# Revit family: Sanitary_Taps-Mixers_hansgrohe_75620XXX-Vivenis-Single-lever-shower-mix_NEW
name_source: partatom
category: Plumbing Fixtures
units: mm (PartAtom-declared; Revit-internal decimal feet)

## family parameters
Always vertical = No
Cut with Voids When Loaded = No
Maintain Annotation Orientation = No
OmniClass Number = 23.31.11.00
OmniClass Title = Faucets
Part Type = Normal
Room Calculation Point = No
Round Connector Dimension = Use Diameter
Shared = No
Work Plane-Based = Yes

## types (5) — shared parameters
Connector Description = Water Inlet 12.7 mm
Date Updated = 2024/11/15
Default Elevation = 1219 mm
Description = Vivenis Single lever shower mixer for exposed installation
Diameter = 13 mm
Manufacturer = Hansgrohe
Model = 75620XXX
Product Page URL = https://www.hansgrohe.com
Product data url = https://bimobject.com
URL = https://www.hansgrohe.com
Version = 2

## per-type parameters (varying)
| type | Material 1 |
| 000 Chrome | Hansgrohe - Metal - 000 Chrome |
| 140 Brushed Bronze | Hansgrohe - Metal - 140 Brushed Bronze |
| 340 Brushed Black Chrome | Hansgrohe - Metal - 340 Brushed Black Chrome |
| 670 Matte Black | Hansgrohe - Metal - 670 Matte Black |
| 700 Matte White | Hansgrohe - Metal - 700 Matte White |

## geometry (parser evidence)
native form markers: Sweep x3
no freeform markers — native parametric forms only
